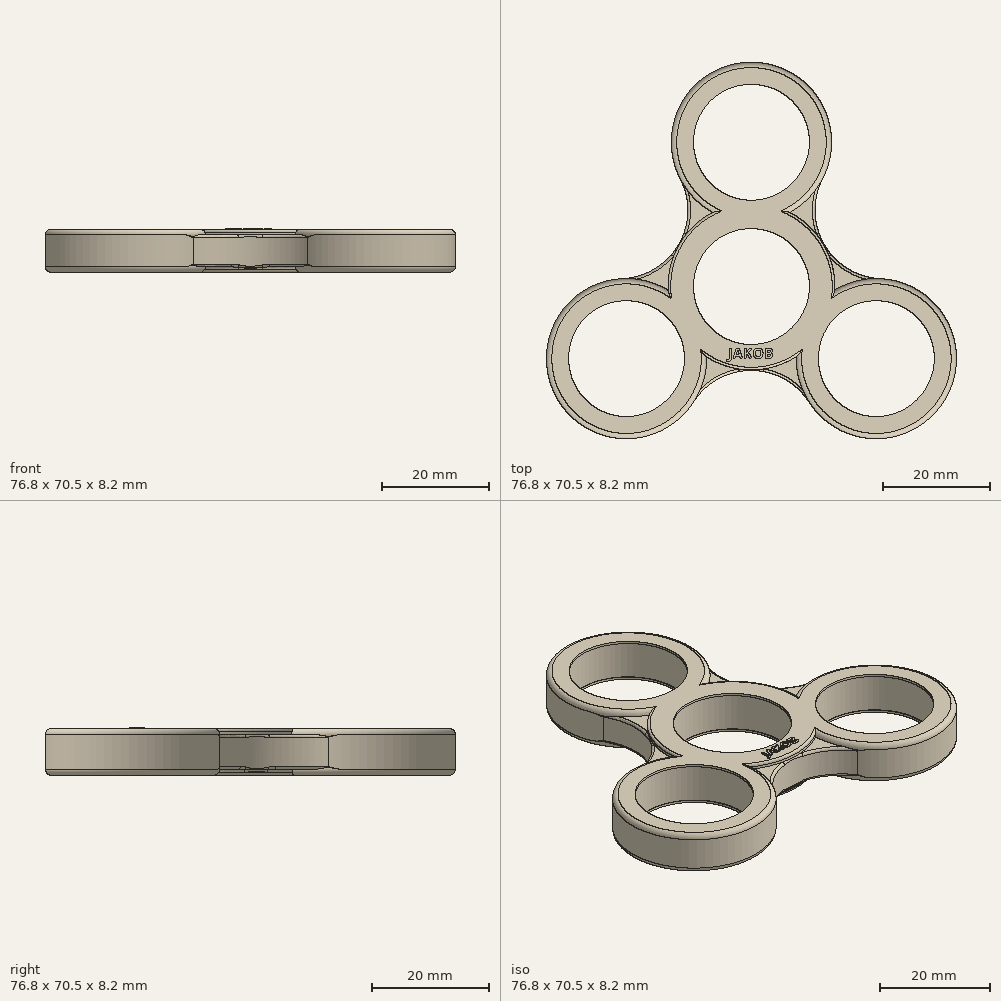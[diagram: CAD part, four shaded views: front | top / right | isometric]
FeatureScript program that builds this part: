
annotation { "Feature Type Name" : "Feature", "Feature Type Description" : "" }
export const myFeature = defineFeature(function(context is Context, id is Id, definition is map)
    precondition{}
    {
        {
            var Q0;
            Q0=qCreatedBy(makeId("Top.planeOp"),FACE);
            var sketch = newSketch(context, id + "F0", { "sketchPlane" : qUnion([Q0])});
            skCircle(sketch, "E0", {"center": v(0, 0) * mm, "radius": 10.85 * mm});
            skCircle(sketch, "E1", {"center": v(0, 27) * mm, "radius": 10.85 * mm});
            skCircle(sketch, "E2.1.0", {"center": v(-23.38, -13.5) * mm, "radius": 10.85 * mm});
            skCircle(sketch, "E2.2.0", {"center": v(23.38, -13.5) * mm, "radius": 10.85 * mm});
            skArc(sketch, "E3", {"start": v(7.22, 13.85) * mm, "mid": v(0, 42) * mm, "end": v(-7.22, 13.85) * mm});
            skArc(sketch, "E4.1.0", {"start": v(8.39, -13.18) * mm, "mid": v(36.37, -21) * mm, "end": v(15.61, -0.67) * mm});
            skArc(sketch, "E4.2.0", {"start": v(-15.61, -0.67) * mm, "mid": v(-36.37, -21) * mm, "end": v(-8.39, -13.18) * mm});
            skArc(sketch, "E5", {"start": v(-8.39, -13.18) * mm, "mid": v(0, -15.62) * mm, "end": v(8.39, -13.18) * mm});
            skArc(sketch, "E6", {"start": v(-24.08, 1.48) * mm, "mid": v(-13.61, 7.86) * mm, "end": v(-13.33, 20.12) * mm});
            skArc(sketch, "E7", {"start": v(10.76, -21.6) * mm, "mid": v(0, -15.72) * mm, "end": v(-10.76, -21.6) * mm});
            skArc(sketch, "E8", {"start": v(13.33, 20.12) * mm, "mid": v(13.61, 7.86) * mm, "end": v(24.08, 1.48) * mm});
            skPoint(sketch, "E9.orphan", {"position": v(-13, 34.5) * mm});
            skPoint(sketch, "E10.orphan", {"position": v(-36.37, -6) * mm});
            skPoint(sketch, "E11.orphan", {"position": v(13, 34.5) * mm});
            skPoint(sketch, "E12.2.0.start.orphan", {"position": v(36.37, -6) * mm});
            skPoint(sketch, "E13.orphan", {"position": v(23.38, -28.5) * mm});
            skPoint(sketch, "E12.1.0.start.orphan", {"position": v(-23.38, -28.5) * mm});
            skArc(sketch, "E14.trimOffspring", {"start": v(15.61, -0.67) * mm, "mid": v(13.53, 7.81) * mm, "end": v(7.22, 13.85) * mm});
            skArc(sketch, "E15.trimOffspring", {"start": v(-7.22, 13.85) * mm, "mid": v(-13.53, 7.81) * mm, "end": v(-15.61, -0.67) * mm});
            skCircle(sketch, "E16", {"center": v(23.38, -13.5) * mm, "radius": 10.95 * mm});
            skCircle(sketch, "E17", {"center": v(-23.38, -13.5) * mm, "radius": 10.95 * mm});
            skCircle(sketch, "E18", {"center": v(0, 0) * mm, "radius": 10.95 * mm});
            skCircle(sketch, "E19", {"center": v(0, 27) * mm, "radius": 10.95 * mm});
            skSolve(sketch);
        }
        {
            var Q0;
            Q0=makeQuery(id+"F0.imprint","IMPRINT",FACE,{"disambiguationData":[TD([[makeQuery(id+"F0.imprint","IMPRINT",EDGE,{"derivedFrom":sQuery(id+"F0.wireOp",EDGE,"E2.1.0")}),-1.0]])]});
            var Q1;
            Q1=makeQuery(id+"F0.imprint","IMPRINT",FACE,{"disambiguationData":[TD([[makeQuery(id+"F0.imprint","IMPRINT",EDGE,{"derivedFrom":sQuery(id+"F0.wireOp",EDGE,"E0")}),-1.0]])]});
            var Q2;
            Q2=makeQuery(id+"F0.imprint","IMPRINT",FACE,{"disambiguationData":[TD([[makeQuery(id+"F0.imprint","IMPRINT",EDGE,{"derivedFrom":sQuery(id+"F0.wireOp",EDGE,"E1")}),-1.0]])]});
            var Q3;
            {var subQ0=sQuery(id+"F0.wireOp",EDGE,"E3");var subQ1=sQuery(id+"F0.wireOp",EDGE,"KJlQqC9l-gusD-toYh-YzLE-zyJcLNbmcpUm");var subQ2=makeQuery(id+"F0.imprint","INTERSECT",VERTEX,{"derivedFrom":[subQ1,subQ0]});Q3=makeQuery(id+"F0.imprint","IMPRINT",FACE,{"disambiguationData":[TD([[makeQuery(id+"F0.imprint","IMPRINT",EDGE,{"disambiguationData":[TD([[subQ2,1.0]])],"derivedFrom":subQ1}),1.0]])]});}
            var Q4;
            {var subQ0=sQuery(id+"F0.wireOp",EDGE,"E3");var subQ1=sQuery(id+"F0.wireOp",EDGE,"KJlQqC9l-gusD-toYh-YzLE-zyJcLNbmcpUm");var subQ2=makeQuery(id+"F0.imprint","INTERSECT",VERTEX,{"derivedFrom":[subQ1,subQ0]});Q4=makeQuery(id+"F0.imprint","IMPRINT",FACE,{"disambiguationData":[TD([[makeQuery(id+"F0.imprint","IMPRINT",EDGE,{"disambiguationData":[TD([[subQ2,1.0]])],"derivedFrom":subQ1}),-1.0]])]});}
            var Q5;
            {var subQ0=sQuery(id+"F0.wireOp",EDGE,"E5");var subQ1=sQuery(id+"F0.wireOp",EDGE,"E4.2.0");var subQ2=makeQuery(id+"F0.imprint","INTERSECT",VERTEX,{"disambiguationData":[OD(0.0)],"derivedFrom":[subQ1,subQ0]});Q5=makeQuery(id+"F0.imprint","IMPRINT",FACE,{"disambiguationData":[TD([[makeQuery(id+"F0.imprint","IMPRINT",EDGE,{"disambiguationData":[TD([[subQ2,-1.0]])],"derivedFrom":subQ1}),1.0]])]});}
            var Q6;
            Q6=makeQuery(id+"F0.imprint","IMPRINT",FACE,{"disambiguationData":[TD([[makeQuery(id+"F0.imprint","IMPRINT",EDGE,{"derivedFrom":sQuery(id+"F0.wireOp",EDGE,"E2.2.0")}),-1.0]])]});
            var Q7;
            {var subQ0=sQuery(id+"F0.wireOp",EDGE,"E5");var subQ1=sQuery(id+"F0.wireOp",EDGE,"E4.1.0");var subQ2=makeQuery(id+"F0.imprint","INTERSECT",VERTEX,{"disambiguationData":[OD(0.0)],"derivedFrom":[subQ1,subQ0]});Q7=makeQuery(id+"F0.imprint","IMPRINT",FACE,{"disambiguationData":[TD([[makeQuery(id+"F0.imprint","IMPRINT",EDGE,{"disambiguationData":[TD([[subQ2,-1.0]])],"derivedFrom":subQ1}),1.0]])]});}
            extrude(context, id + "F1", {"entities" : qUnion([Q0, Q1, Q2, Q3, Q4, Q5, Q6, Q7]), "endBound" : BoundingType.SYMMETRIC, "depth" : 8 * mm, "offsetDistance" : 25 * mm});
        }
        {
            var Q0;
            {var subQ0=sQuery(id+"F0.wireOp",EDGE,"E7");Q0=makeQuery(id+"F0.imprint","IMPRINT",FACE,{"disambiguationData":[TD([[makeQuery(id+"F0.imprint","IMPRINT",EDGE,{"derivedFrom":subQ0}),-1.0]])]});}
            var Q1;
            {var subQ0=sQuery(id+"F0.wireOp",EDGE,"E6");Q1=makeQuery(id+"F0.imprint","IMPRINT",FACE,{"disambiguationData":[TD([[makeQuery(id+"F0.imprint","IMPRINT",EDGE,{"derivedFrom":subQ0}),-1.0]])]});}
            var Q2;
            {var subQ0=sQuery(id+"F0.wireOp",EDGE,"E8");Q2=makeQuery(id+"F0.imprint","IMPRINT",FACE,{"disambiguationData":[TD([[makeQuery(id+"F0.imprint","IMPRINT",EDGE,{"derivedFrom":subQ0}),-1.0]])]});}
            extrude(context, id + "F2", {"entities" : qUnion([Q0, Q1, Q2]), "operationType" : NewBodyOperationType.ADD, "endBound" : BoundingType.SYMMETRIC, "depth" : 6 * mm, "offsetDistance" : 25 * mm});
        }
        {
            var Q0;
            Q0=makeQuery(id+"F1.opExtrude","CAP_EDGE",EDGE,{"disambiguationData":[OSD([sQuery(id+"F0.wireOp",EDGE,"E15.trimOffspring")])],"isStart":true});
            var Q1;
            Q1=makeQuery(id+"F2.opExtrude","CAP_EDGE",EDGE,{"disambiguationData":[OSD([sQuery(id+"F0.wireOp",EDGE,"E15.trimOffspring")])],"isStart":true});
            var Q2;
            Q2=makeQuery(id+"F1.opExtrude","CAP_EDGE",EDGE,{"disambiguationData":[OSD([sQuery(id+"F0.wireOp",EDGE,"E5")])],"isStart":true});
            var Q3;
            Q3=makeQuery(id+"F2.opExtrude","CAP_EDGE",EDGE,{"disambiguationData":[OSD([sQuery(id+"F0.wireOp",EDGE,"E5")])],"isStart":true});
            var Q4;
            Q4=makeQuery(id+"F1.opExtrude","CAP_EDGE",EDGE,{"disambiguationData":[OSD([sQuery(id+"F0.wireOp",EDGE,"E14.trimOffspring")])],"isStart":true});
            var Q5;
            Q5=makeQuery(id+"F2.opExtrude","CAP_EDGE",EDGE,{"disambiguationData":[OSD([sQuery(id+"F0.wireOp",EDGE,"E14.trimOffspring")])],"isStart":true});
            fillet(context, id + "F3", {"entities" : qUnion([Q0, Q1, Q2, Q3, Q4, Q5]), "radius" : 0.5 * mm, "rho" : 0.5, "crossSection" : FilletCrossSection.CONIC, "allowEdgeOverflow" : false});
        }
        {
            var Q0;
            Q0=makeQuery(id+"F1.opExtrude","CAP_EDGE",EDGE,{"disambiguationData":[OSD([sQuery(id+"F0.wireOp",EDGE,"E5")])],"isStart":false});
            var Q1;
            Q1=makeQuery(id+"F2.opExtrude","CAP_EDGE",EDGE,{"disambiguationData":[OSD([sQuery(id+"F0.wireOp",EDGE,"E5")])],"isStart":false});
            var Q2;
            Q2=makeQuery(id+"F1.opExtrude","CAP_EDGE",EDGE,{"disambiguationData":[OSD([sQuery(id+"F0.wireOp",EDGE,"E14.trimOffspring")])],"isStart":false});
            var Q3;
            Q3=makeQuery(id+"F2.opExtrude","CAP_EDGE",EDGE,{"disambiguationData":[OSD([sQuery(id+"F0.wireOp",EDGE,"E14.trimOffspring")])],"isStart":false});
            var Q4;
            Q4=makeQuery(id+"F1.opExtrude","CAP_EDGE",EDGE,{"disambiguationData":[OSD([sQuery(id+"F0.wireOp",EDGE,"E15.trimOffspring")])],"isStart":false});
            var Q5;
            Q5=makeQuery(id+"F2.opExtrude","CAP_EDGE",EDGE,{"disambiguationData":[OSD([sQuery(id+"F0.wireOp",EDGE,"E15.trimOffspring")])],"isStart":false});
            fillet(context, id + "F4", {"entities" : qUnion([Q0, Q1, Q2, Q3, Q4, Q5]), "radius" : 0.5 * mm, "rho" : 0.5, "crossSection" : FilletCrossSection.CONIC, "allowEdgeOverflow" : false});
        }
        {
            var Q0;
            Q0=makeQuery(id+"F1.opExtrude","CAP_EDGE",EDGE,{"disambiguationData":[OSD([sQuery(id+"F0.wireOp",EDGE,"E4.1.0")])],"isStart":false});
            var Q1;
            Q1=makeQuery(id+"F1.opExtrude","CAP_EDGE",EDGE,{"disambiguationData":[OSD([sQuery(id+"F0.wireOp",EDGE,"E3")])],"isStart":false});
            var Q2;
            Q2=makeQuery(id+"F1.opExtrude","CAP_EDGE",EDGE,{"disambiguationData":[OSD([sQuery(id+"F0.wireOp",EDGE,"E4.2.0")])],"isStart":false});
            var Q3;
            Q3=makeQuery(id+"F1.opExtrude","CAP_EDGE",EDGE,{"disambiguationData":[OSD([sQuery(id+"F0.wireOp",EDGE,"E4.2.0")])],"isStart":true});
            var Q4;
            Q4=makeQuery(id+"F1.opExtrude","CAP_EDGE",EDGE,{"disambiguationData":[OSD([sQuery(id+"F0.wireOp",EDGE,"E4.1.0")])],"isStart":true});
            var Q5;
            Q5=makeQuery(id+"F1.opExtrude","CAP_EDGE",EDGE,{"disambiguationData":[OSD([sQuery(id+"F0.wireOp",EDGE,"E3")])],"isStart":true});
            fillet(context, id + "F5", {"entities" : qUnion([Q0, Q1, Q2, Q3, Q4, Q5]), "radius" : 1 * mm, "allowEdgeOverflow" : false});
        }
        {
            var Q0;
            Q0=makeQuery(id+"F2.opExtrude","SWEPT_FACE",FACE,{"disambiguationData":[OSD([sQuery(id+"F0.wireOp",EDGE,"E8")])]});
            var Q1;
            Q1=makeQuery(id+"F2.opExtrude","SWEPT_FACE",FACE,{"disambiguationData":[OSD([sQuery(id+"F0.wireOp",EDGE,"E6")])]});
            var Q2;
            Q2=makeQuery(id+"F2.opExtrude","SWEPT_FACE",FACE,{"disambiguationData":[OSD([sQuery(id+"F0.wireOp",EDGE,"E7")])]});
            fillet(context, id + "F6", {"entities" : qUnion([Q0, Q1, Q2]), "radius" : .5 * mm, "tangentPropagation" : true, "allowEdgeOverflow" : false});
        }
        {
            var Q0;
            Q0=makeQuery(id+"F0.imprint","IMPRINT",FACE,{"disambiguationData":[TD([[makeQuery(id+"F0.imprint","IMPRINT",EDGE,{"derivedFrom":sQuery(id+"F0.wireOp",EDGE,"E19")}),1.0]])]});
            var Q1;
            Q1=makeQuery(id+"F0.imprint","IMPRINT",FACE,{"disambiguationData":[TD([[makeQuery(id+"F0.imprint","IMPRINT",EDGE,{"derivedFrom":sQuery(id+"F0.wireOp",EDGE,"E18")}),1.0]])]});
            var Q2;
            Q2=makeQuery(id+"F0.imprint","IMPRINT",FACE,{"disambiguationData":[TD([[makeQuery(id+"F0.imprint","IMPRINT",EDGE,{"derivedFrom":sQuery(id+"F0.wireOp",EDGE,"E16")}),1.0]])]});
            var Q3;
            Q3=makeQuery(id+"F0.imprint","IMPRINT",FACE,{"disambiguationData":[TD([[makeQuery(id+"F0.imprint","IMPRINT",EDGE,{"derivedFrom":sQuery(id+"F0.wireOp",EDGE,"E17")}),1.0]])]});
            extrude(context, id + "F7", {"entities" : qUnion([Q0, Q1, Q2, Q3]), "endBound" : BoundingType.SYMMETRIC, "depth" : 7.1 * mm, "offsetDistance" : 25 * mm});
        }
        {
            var Q0;
            Q0=makeQuery(id+"F7.opExtrude","SWEPT_BODY",BODY,{"disambiguationData":[OSD([sQuery(id+"F0.wireOp",EDGE,"E16")])]});
            var Q1;
            Q1=makeQuery(id+"F7.opExtrude","SWEPT_BODY",BODY,{"disambiguationData":[OSD([sQuery(id+"F0.wireOp",EDGE,"E17")])]});
            var Q2;
            Q2=makeQuery(id+"F7.opExtrude","SWEPT_BODY",BODY,{"disambiguationData":[OSD([sQuery(id+"F0.wireOp",EDGE,"E18")])]});
            var Q3;
            Q3=makeQuery(id+"F7.opExtrude","SWEPT_BODY",BODY,{"disambiguationData":[OSD([sQuery(id+"F0.wireOp",EDGE,"E19")])]});
            var Q4;
            Q4=makeQuery(id+"F1.opExtrude","SWEPT_BODY",BODY,{"disambiguationData":[OSD([sQuery(id+"F0.wireOp",EDGE,"E0"),sQuery(id+"F0.wireOp",EDGE,"E1"),sQuery(id+"F0.wireOp",EDGE,"E2.1.0"),sQuery(id+"F0.wireOp",EDGE,"E2.2.0"),sQuery(id+"F0.wireOp",EDGE,"E3"),sQuery(id+"F0.wireOp",EDGE,"E4.1.0"),sQuery(id+"F0.wireOp",EDGE,"E4.2.0"),sQuery(id+"F0.wireOp",EDGE,"E5"),sQuery(id+"F0.wireOp",EDGE,"E14.trimOffspring"),sQuery(id+"F0.wireOp",EDGE,"E15.trimOffspring"),sQuery(id+"F0.wireOp",EDGE,"f471b002-4030-4226-8843-a168e7eb6244.sketch_text.stroke-7"),sQuery(id+"F0.wireOp",EDGE,"f471b002-4030-4226-8843-a168e7eb6244.sketch_text.stroke-8"),sQuery(id+"F0.wireOp",EDGE,"f471b002-4030-4226-8843-a168e7eb6244.sketch_text.stroke-9"),sQuery(id+"F0.wireOp",EDGE,"f471b002-4030-4226-8843-a168e7eb6244.sketch_text.stroke-10"),sQuery(id+"F0.wireOp",EDGE,"f471b002-4030-4226-8843-a168e7eb6244.sketch_text.stroke-11"),sQuery(id+"F0.wireOp",EDGE,"f471b002-4030-4226-8843-a168e7eb6244.sketch_text.stroke-12"),sQuery(id+"F0.wireOp",EDGE,"f471b002-4030-4226-8843-a168e7eb6244.sketch_text.stroke-13"),sQuery(id+"F0.wireOp",EDGE,"f471b002-4030-4226-8843-a168e7eb6244.sketch_text.stroke-14"),sQuery(id+"F0.wireOp",EDGE,"f471b002-4030-4226-8843-a168e7eb6244.sketch_text.stroke-15"),sQuery(id+"F0.wireOp",EDGE,"f471b002-4030-4226-8843-a168e7eb6244.sketch_text.stroke-16"),sQuery(id+"F0.wireOp",EDGE,"f471b002-4030-4226-8843-a168e7eb6244.sketch_text.stroke-17"),sQuery(id+"F0.wireOp",EDGE,"f471b002-4030-4226-8843-a168e7eb6244.sketch_text.stroke-18"),sQuery(id+"F0.wireOp",EDGE,"f471b002-4030-4226-8843-a168e7eb6244.sketch_text.stroke-19"),sQuery(id+"F0.wireOp",EDGE,"f471b002-4030-4226-8843-a168e7eb6244.sketch_text.stroke-20"),sQuery(id+"F0.wireOp",EDGE,"f471b002-4030-4226-8843-a168e7eb6244.sketch_text.stroke-21"),sQuery(id+"F0.wireOp",EDGE,"f471b002-4030-4226-8843-a168e7eb6244.sketch_text.stroke-22"),sQuery(id+"F0.wireOp",EDGE,"f471b002-4030-4226-8843-a168e7eb6244.sketch_text.stroke-23"),sQuery(id+"F0.wireOp",EDGE,"f471b002-4030-4226-8843-a168e7eb6244.sketch_text.stroke-28"),sQuery(id+"F0.wireOp",EDGE,"f471b002-4030-4226-8843-a168e7eb6244.sketch_text.stroke-29"),sQuery(id+"F0.wireOp",EDGE,"f471b002-4030-4226-8843-a168e7eb6244.sketch_text.stroke-30"),sQuery(id+"F0.wireOp",EDGE,"f471b002-4030-4226-8843-a168e7eb6244.sketch_text.stroke-31"),sQuery(id+"F0.wireOp",EDGE,"f471b002-4030-4226-8843-a168e7eb6244.sketch_text.stroke-32"),sQuery(id+"F0.wireOp",EDGE,"f471b002-4030-4226-8843-a168e7eb6244.sketch_text.stroke-33"),sQuery(id+"F0.wireOp",EDGE,"f471b002-4030-4226-8843-a168e7eb6244.sketch_text.stroke-34"),sQuery(id+"F0.wireOp",EDGE,"f471b002-4030-4226-8843-a168e7eb6244.sketch_text.stroke-35"),sQuery(id+"F0.wireOp",EDGE,"f471b002-4030-4226-8843-a168e7eb6244.sketch_text.stroke-36"),sQuery(id+"F0.wireOp",EDGE,"f471b002-4030-4226-8843-a168e7eb6244.sketch_text.stroke-37"),sQuery(id+"F0.wireOp",EDGE,"f471b002-4030-4226-8843-a168e7eb6244.sketch_text.stroke-38"),sQuery(id+"F0.wireOp",EDGE,"f471b002-4030-4226-8843-a168e7eb6244.sketch_text.stroke-39"),sQuery(id+"F0.wireOp",EDGE,"f471b002-4030-4226-8843-a168e7eb6244.sketch_text.stroke-40"),sQuery(id+"F0.wireOp",EDGE,"f471b002-4030-4226-8843-a168e7eb6244.sketch_text.stroke-41"),sQuery(id+"F0.wireOp",EDGE,"f471b002-4030-4226-8843-a168e7eb6244.sketch_text.stroke-42"),sQuery(id+"F0.wireOp",EDGE,"f471b002-4030-4226-8843-a168e7eb6244.sketch_text.stroke-43"),sQuery(id+"F0.wireOp",EDGE,"f471b002-4030-4226-8843-a168e7eb6244.sketch_text.stroke-44"),sQuery(id+"F0.wireOp",EDGE,"f471b002-4030-4226-8843-a168e7eb6244.sketch_text.stroke-45"),sQuery(id+"F0.wireOp",EDGE,"f471b002-4030-4226-8843-a168e7eb6244.sketch_text.stroke-46"),sQuery(id+"F0.wireOp",EDGE,"f471b002-4030-4226-8843-a168e7eb6244.sketch_text.stroke-47"),sQuery(id+"F0.wireOp",EDGE,"f471b002-4030-4226-8843-a168e7eb6244.sketch_text.stroke-48"),sQuery(id+"F0.wireOp",EDGE,"f471b002-4030-4226-8843-a168e7eb6244.sketch_text.stroke-49"),sQuery(id+"F0.wireOp",EDGE,"f471b002-4030-4226-8843-a168e7eb6244.sketch_text.stroke-50"),sQuery(id+"F0.wireOp",EDGE,"f471b002-4030-4226-8843-a168e7eb6244.sketch_text.stroke-51"),sQuery(id+"F0.wireOp",EDGE,"f471b002-4030-4226-8843-a168e7eb6244.sketch_text.stroke-52"),sQuery(id+"F0.wireOp",EDGE,"f471b002-4030-4226-8843-a168e7eb6244.sketch_text.stroke-53"),sQuery(id+"F0.wireOp",EDGE,"f471b002-4030-4226-8843-a168e7eb6244.sketch_text.stroke-54"),sQuery(id+"F0.wireOp",EDGE,"f471b002-4030-4226-8843-a168e7eb6244.sketch_text.stroke-55"),sQuery(id+"F0.wireOp",EDGE,"f471b002-4030-4226-8843-a168e7eb6244.sketch_text.stroke-56"),sQuery(id+"F0.wireOp",EDGE,"f471b002-4030-4226-8843-a168e7eb6244.sketch_text.stroke-57"),sQuery(id+"F0.wireOp",EDGE,"f471b002-4030-4226-8843-a168e7eb6244.sketch_text.stroke-58"),sQuery(id+"F0.wireOp",EDGE,"f471b002-4030-4226-8843-a168e7eb6244.sketch_text.stroke-59"),sQuery(id+"F0.wireOp",EDGE,"f471b002-4030-4226-8843-a168e7eb6244.sketch_text.stroke-60"),sQuery(id+"F0.wireOp",EDGE,"f471b002-4030-4226-8843-a168e7eb6244.sketch_text.stroke-74"),sQuery(id+"F0.wireOp",EDGE,"f471b002-4030-4226-8843-a168e7eb6244.sketch_text.stroke-75"),sQuery(id+"F0.wireOp",EDGE,"f471b002-4030-4226-8843-a168e7eb6244.sketch_text.stroke-76"),sQuery(id+"F0.wireOp",EDGE,"f471b002-4030-4226-8843-a168e7eb6244.sketch_text.stroke-77"),sQuery(id+"F0.wireOp",EDGE,"f471b002-4030-4226-8843-a168e7eb6244.sketch_text.stroke-78"),sQuery(id+"F0.wireOp",EDGE,"f471b002-4030-4226-8843-a168e7eb6244.sketch_text.stroke-79"),sQuery(id+"F0.wireOp",EDGE,"f471b002-4030-4226-8843-a168e7eb6244.sketch_text.stroke-80"),sQuery(id+"F0.wireOp",EDGE,"f471b002-4030-4226-8843-a168e7eb6244.sketch_text.stroke-81"),sQuery(id+"F0.wireOp",EDGE,"f471b002-4030-4226-8843-a168e7eb6244.sketch_text.stroke-86"),sQuery(id+"F0.wireOp",EDGE,"f471b002-4030-4226-8843-a168e7eb6244.sketch_text.stroke-87"),sQuery(id+"F0.wireOp",EDGE,"f471b002-4030-4226-8843-a168e7eb6244.sketch_text.stroke-88"),sQuery(id+"F0.wireOp",EDGE,"f471b002-4030-4226-8843-a168e7eb6244.sketch_text.stroke-89"),sQuery(id+"F0.wireOp",EDGE,"f471b002-4030-4226-8843-a168e7eb6244.sketch_text.stroke-90"),sQuery(id+"F0.wireOp",EDGE,"f471b002-4030-4226-8843-a168e7eb6244.sketch_text.stroke-91"),sQuery(id+"F0.wireOp",EDGE,"f471b002-4030-4226-8843-a168e7eb6244.sketch_text.stroke-92"),sQuery(id+"F0.wireOp",EDGE,"f471b002-4030-4226-8843-a168e7eb6244.sketch_text.stroke-93"),sQuery(id+"F0.wireOp",EDGE,"f471b002-4030-4226-8843-a168e7eb6244.sketch_text.stroke-94"),sQuery(id+"F0.wireOp",EDGE,"f471b002-4030-4226-8843-a168e7eb6244.sketch_text.stroke-95"),sQuery(id+"F0.wireOp",EDGE,"f471b002-4030-4226-8843-a168e7eb6244.sketch_text.stroke-96"),sQuery(id+"F0.wireOp",EDGE,"f471b002-4030-4226-8843-a168e7eb6244.sketch_text.stroke-97"),sQuery(id+"F0.wireOp",EDGE,"f471b002-4030-4226-8843-a168e7eb6244.sketch_text.stroke-98"),sQuery(id+"F0.wireOp",EDGE,"f471b002-4030-4226-8843-a168e7eb6244.sketch_text.stroke-99"),sQuery(id+"F0.wireOp",EDGE,"f471b002-4030-4226-8843-a168e7eb6244.sketch_text.stroke-100"),sQuery(id+"F0.wireOp",EDGE,"f471b002-4030-4226-8843-a168e7eb6244.sketch_text.stroke-101"),sQuery(id+"F0.wireOp",EDGE,"f471b002-4030-4226-8843-a168e7eb6244.sketch_text.stroke-102"),sQuery(id+"F0.wireOp",EDGE,"f471b002-4030-4226-8843-a168e7eb6244.sketch_text.stroke-103"),sQuery(id+"F0.wireOp",EDGE,"f471b002-4030-4226-8843-a168e7eb6244.sketch_text.stroke-104"),sQuery(id+"F0.wireOp",EDGE,"f471b002-4030-4226-8843-a168e7eb6244.sketch_text.stroke-105"),sQuery(id+"F0.wireOp",EDGE,"f471b002-4030-4226-8843-a168e7eb6244.sketch_text.stroke-106"),sQuery(id+"F0.wireOp",EDGE,"f471b002-4030-4226-8843-a168e7eb6244.sketch_text.stroke-107"),sQuery(id+"F0.wireOp",EDGE,"f471b002-4030-4226-8843-a168e7eb6244.sketch_text.stroke-108"),sQuery(id+"F0.wireOp",EDGE,"f471b002-4030-4226-8843-a168e7eb6244.sketch_text.stroke-109"),sQuery(id+"F0.wireOp",EDGE,"f471b002-4030-4226-8843-a168e7eb6244.sketch_text.stroke-110"),sQuery(id+"F0.wireOp",EDGE,"f471b002-4030-4226-8843-a168e7eb6244.sketch_text.stroke-111"),sQuery(id+"F0.wireOp",EDGE,"f471b002-4030-4226-8843-a168e7eb6244.sketch_text.stroke-112"),sQuery(id+"F0.wireOp",EDGE,"f471b002-4030-4226-8843-a168e7eb6244.sketch_text.stroke-113"),sQuery(id+"F0.wireOp",EDGE,"f471b002-4030-4226-8843-a168e7eb6244.sketch_text.stroke-114"),sQuery(id+"F0.wireOp",EDGE,"f471b002-4030-4226-8843-a168e7eb6244.sketch_text.stroke-115"),sQuery(id+"F0.wireOp",EDGE,"f471b002-4030-4226-8843-a168e7eb6244.sketch_text.stroke-116"),sQuery(id+"F0.wireOp",EDGE,"f471b002-4030-4226-8843-a168e7eb6244.sketch_text.stroke-117"),sQuery(id+"F0.wireOp",EDGE,"f471b002-4030-4226-8843-a168e7eb6244.sketch_text.stroke-118"),sQuery(id+"F0.wireOp",EDGE,"f471b002-4030-4226-8843-a168e7eb6244.sketch_text.stroke-119"),sQuery(id+"F0.wireOp",EDGE,"f471b002-4030-4226-8843-a168e7eb6244.sketch_text.stroke-120"),sQuery(id+"F0.wireOp",EDGE,"f471b002-4030-4226-8843-a168e7eb6244.sketch_text.stroke-121"),sQuery(id+"F0.wireOp",EDGE,"f471b002-4030-4226-8843-a168e7eb6244.sketch_text.stroke-122"),sQuery(id+"F0.wireOp",EDGE,"f471b002-4030-4226-8843-a168e7eb6244.sketch_text.stroke-123"),sQuery(id+"F0.wireOp",EDGE,"f471b002-4030-4226-8843-a168e7eb6244.sketch_text.stroke-124"),sQuery(id+"F0.wireOp",EDGE,"f471b002-4030-4226-8843-a168e7eb6244.sketch_text.stroke-125"),sQuery(id+"F0.wireOp",EDGE,"f471b002-4030-4226-8843-a168e7eb6244.sketch_text.stroke-126"),sQuery(id+"F0.wireOp",EDGE,"f471b002-4030-4226-8843-a168e7eb6244.sketch_text.stroke-127"),sQuery(id+"F0.wireOp",EDGE,"f471b002-4030-4226-8843-a168e7eb6244.sketch_text.stroke-128"),sQuery(id+"F0.wireOp",EDGE,"f471b002-4030-4226-8843-a168e7eb6244.sketch_text.stroke-129"),sQuery(id+"F0.wireOp",EDGE,"f471b002-4030-4226-8843-a168e7eb6244.sketch_text.stroke-130"),sQuery(id+"F0.wireOp",EDGE,"f471b002-4030-4226-8843-a168e7eb6244.sketch_text.stroke-131"),sQuery(id+"F0.wireOp",EDGE,"f471b002-4030-4226-8843-a168e7eb6244.sketch_text.stroke-132"),sQuery(id+"F0.wireOp",EDGE,"f471b002-4030-4226-8843-a168e7eb6244.sketch_text.stroke-133"),sQuery(id+"F0.wireOp",EDGE,"f471b002-4030-4226-8843-a168e7eb6244.sketch_text.stroke-134"),sQuery(id+"F0.wireOp",EDGE,"f471b002-4030-4226-8843-a168e7eb6244.sketch_text.stroke-135"),sQuery(id+"F0.wireOp",EDGE,"f471b002-4030-4226-8843-a168e7eb6244.sketch_text.stroke-136"),sQuery(id+"F0.wireOp",EDGE,"f471b002-4030-4226-8843-a168e7eb6244.sketch_text.stroke-137"),sQuery(id+"F0.wireOp",EDGE,"f471b002-4030-4226-8843-a168e7eb6244.sketch_text.stroke-138"),sQuery(id+"F0.wireOp",EDGE,"f471b002-4030-4226-8843-a168e7eb6244.sketch_text.stroke-139"),sQuery(id+"F0.wireOp",EDGE,"f471b002-4030-4226-8843-a168e7eb6244.sketch_text.stroke-140"),sQuery(id+"F0.wireOp",EDGE,"f471b002-4030-4226-8843-a168e7eb6244.sketch_text.stroke-141"),sQuery(id+"F0.wireOp",EDGE,"f471b002-4030-4226-8843-a168e7eb6244.sketch_text.stroke-142"),sQuery(id+"F0.wireOp",EDGE,"f471b002-4030-4226-8843-a168e7eb6244.sketch_text.stroke-143"),sQuery(id+"F0.wireOp",EDGE,"f471b002-4030-4226-8843-a168e7eb6244.sketch_text.stroke-144"),sQuery(id+"F0.wireOp",EDGE,"f471b002-4030-4226-8843-a168e7eb6244.sketch_text.stroke-145"),sQuery(id+"F0.wireOp",EDGE,"f471b002-4030-4226-8843-a168e7eb6244.sketch_text.stroke-146"),sQuery(id+"F0.wireOp",EDGE,"f471b002-4030-4226-8843-a168e7eb6244.sketch_text.stroke-147"),sQuery(id+"F0.wireOp",EDGE,"f471b002-4030-4226-8843-a168e7eb6244.sketch_text.stroke-148"),sQuery(id+"F0.wireOp",EDGE,"f471b002-4030-4226-8843-a168e7eb6244.sketch_text.stroke-149"),sQuery(id+"F0.wireOp",EDGE,"f471b002-4030-4226-8843-a168e7eb6244.sketch_text.stroke-150"),sQuery(id+"F0.wireOp",EDGE,"f471b002-4030-4226-8843-a168e7eb6244.sketch_text.stroke-151"),sQuery(id+"F0.wireOp",EDGE,"f471b002-4030-4226-8843-a168e7eb6244.sketch_text.stroke-152"),sQuery(id+"F0.wireOp",EDGE,"f471b002-4030-4226-8843-a168e7eb6244.sketch_text.stroke-153"),sQuery(id+"F0.wireOp",EDGE,"f471b002-4030-4226-8843-a168e7eb6244.sketch_text.stroke-154"),sQuery(id+"F0.wireOp",EDGE,"f471b002-4030-4226-8843-a168e7eb6244.sketch_text.stroke-155"),sQuery(id+"F0.wireOp",EDGE,"f471b002-4030-4226-8843-a168e7eb6244.sketch_text.stroke-156"),sQuery(id+"F0.wireOp",EDGE,"f471b002-4030-4226-8843-a168e7eb6244.sketch_text.stroke-157"),sQuery(id+"F0.wireOp",EDGE,"f471b002-4030-4226-8843-a168e7eb6244.sketch_text.stroke-158"),sQuery(id+"F0.wireOp",EDGE,"f471b002-4030-4226-8843-a168e7eb6244.sketch_text.stroke-159"),sQuery(id+"F0.wireOp",EDGE,"f471b002-4030-4226-8843-a168e7eb6244.sketch_text.stroke-160"),sQuery(id+"F0.wireOp",EDGE,"f471b002-4030-4226-8843-a168e7eb6244.sketch_text.stroke-161"),sQuery(id+"F0.wireOp",EDGE,"f471b002-4030-4226-8843-a168e7eb6244.sketch_text.stroke-162"),sQuery(id+"F0.wireOp",EDGE,"f471b002-4030-4226-8843-a168e7eb6244.sketch_text.stroke-163"),sQuery(id+"F0.wireOp",EDGE,"f471b002-4030-4226-8843-a168e7eb6244.sketch_text.stroke-164"),sQuery(id+"F0.wireOp",EDGE,"f471b002-4030-4226-8843-a168e7eb6244.sketch_text.stroke-165"),sQuery(id+"F0.wireOp",EDGE,"f471b002-4030-4226-8843-a168e7eb6244.sketch_text.stroke-166"),sQuery(id+"F0.wireOp",EDGE,"f471b002-4030-4226-8843-a168e7eb6244.sketch_text.stroke-167"),sQuery(id+"F0.wireOp",EDGE,"f471b002-4030-4226-8843-a168e7eb6244.sketch_text.stroke-168"),sQuery(id+"F0.wireOp",EDGE,"f471b002-4030-4226-8843-a168e7eb6244.sketch_text.stroke-169"),sQuery(id+"F0.wireOp",EDGE,"f471b002-4030-4226-8843-a168e7eb6244.sketch_text.stroke-170")])]});
            booleanBodies(context, id + "F8", {"operationType" : BooleanOperationType.SUBTRACTION, "tools" : qUnion([Q0, Q1, Q2, Q3]), "targets" : qUnion([Q4])});
        }
        {
            var Q0;
            Q0=makeQuery(id+"F1.opExtrude","CAP_FACE",FACE,{"disambiguationData":[OSD([sQuery(id+"F0.wireOp",EDGE,"E0"),sQuery(id+"F0.wireOp",EDGE,"E1"),sQuery(id+"F0.wireOp",EDGE,"E2.1.0"),sQuery(id+"F0.wireOp",EDGE,"E2.2.0"),sQuery(id+"F0.wireOp",EDGE,"E3"),sQuery(id+"F0.wireOp",EDGE,"E4.1.0"),sQuery(id+"F0.wireOp",EDGE,"E4.2.0"),sQuery(id+"F0.wireOp",EDGE,"E5"),sQuery(id+"F0.wireOp",EDGE,"E14.trimOffspring"),sQuery(id+"F0.wireOp",EDGE,"E15.trimOffspring")])],"isStart":false});
            var sketch = newSketch(context, id + "F9", { "sketchPlane" : qUnion([Q0])});
            skText(sketch, "E20", { "text": "JAKOB", "fontName": "OpenSans-Bold.ttf"});
            const initialGuessF9  = {"E20": [-0.0044, -0.0135, 1, 0, 0.00195]};
            skSetInitialGuess(sketch, initialGuessF9);
            skSolve(sketch);
        }
        {
            var Q0;
            Q0 = qSketchRegion(id + "F9", true);
            extrude(context, id + "F10", {"entities" : qUnion([Q0]), "operationType" : NewBodyOperationType.ADD, "depth" : 0.15 * mm, "offsetDistance" : 25 * mm});
        }
    });
